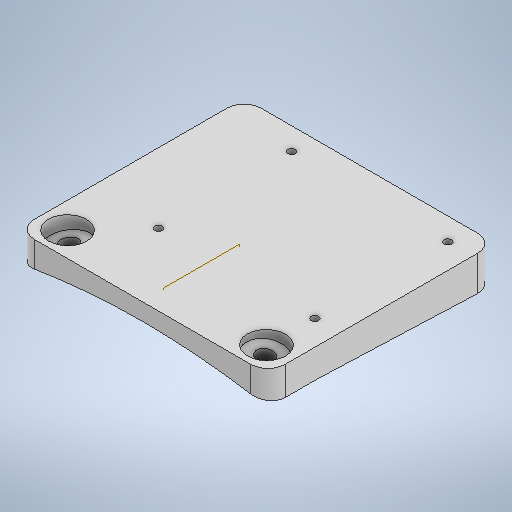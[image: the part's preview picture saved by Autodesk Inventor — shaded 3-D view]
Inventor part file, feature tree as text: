
AUTODESK INVENTOR PART (.ipt)
format: ipt  version: 2025 (Build 290162000, 162)  size: 406,016 bytes
history: native  units: in
note: dims shown in document units (in); Inventor stores cm internally (conversion verified against a paired STEP export)
features: sketch x8, extrude x7, mirror x2, other x2, revolve x1, plane x1, loft x1, fillet x1
ambient origin geometry x8: Origin, YZ Plane, XZ Plane, XY Plane, X Axis, Y Axis, Z Axis, Center Point
bodies: Solid1 (feature_tree)
feature tree (23):
  extrude  "Extrusion1"  Depth=0.25in
  revolve  "Revolution1"  [1 undecoded]
  extrude  "Extrusion2"  Depth=0.0563in
  plane  "Work Plane9"
  mirror  "Mirror1"
  extrude  "Extrusion3"  TaperAngle=90.0deg  [1 undecoded]
  mirror  "Mirror2"
  extrude  "Extrusion4"  TaperAngle=90.0deg  [1 undecoded]
  extrude  "Extrusion5"  Depth=0.6748in
  extrude  "Extrusion6"  TaperAngle=180.0deg  [1 undecoded]
  loft  "Loft1"
  extrude  "Extrusion7"  Depth=0.25in TaperAngle=0.0deg
  fillet  "Fillet1"  Radius=0.356in
  sketch  "Sketch1"  dims[d2=0.25in d3=1.5in]
  sketch  "Sketch2"  dims[d4=1.0in d5=0.0in d6=0.1in]
  sketch  "Sketch3"  dims[d7=0.12in d8=0.0563in]
  sketch  "Sketch5"  dims[d9=0.2in d10=90.0deg]
  sketch  "Sketch6"  dims[d11=0.275in d12=90.0deg]
  sketch  "Sketch7"  dims[d13=0.15in d14=0.6748in]
  sketch  "Sketch8"  dims[d15=0.1in d16=180.0deg]
  other  "Edges1"
  other  "Edges2"
  sketch  "Sketch9"  dims[d17=1.0in d18=0.0in d27=-1.8228in d28=1.0in d29=0.0in d30=0.356in d31=90.0deg d32=0.712in d33=1.0in d34=0.0in d52=2.585in d53=2.585in d54=0.36in d55=0.33in d56=0.11in d57=2.27in d58=1.93in d59=0.11in d60=0.11in d61=0.11in d62=0.2in d63=0.0in d64=0.345in d65=0.099in d66=0.099in d67=0.001in d68=0.0in d69=0.0in d70=90.0deg d71=0.0in d72=90.0deg d73=0.285in d74=0.0in d75=0.25in]
note: 4 required parameter values undecoded (feature->parameter linkage not recoverable at this tier; creation-order binding heuristic only, values carry confidence <= 0.55)